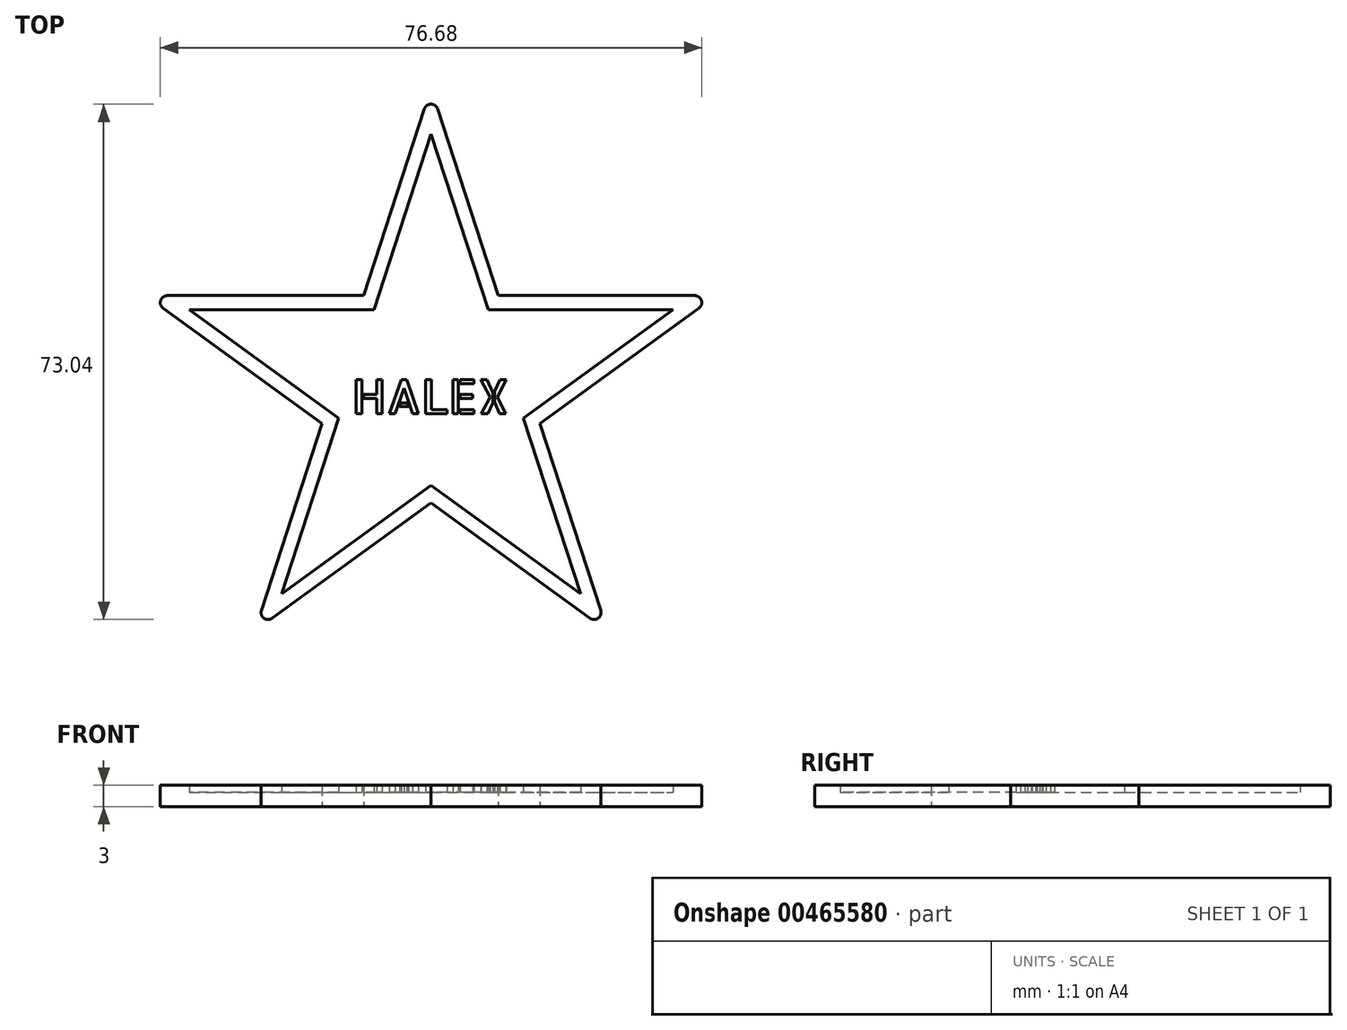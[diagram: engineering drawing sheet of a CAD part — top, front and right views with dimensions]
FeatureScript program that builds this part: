
annotation { "Feature Type Name" : "Feature", "Feature Type Description" : "" }
export const myFeature = defineFeature(function(context is Context, id is Id, definition is map)
    precondition{}
    {
        {
            var Q0;
            Q0=qCreatedBy(makeId("Top.planeOp"),FACE);
            var sketch = newSketch(context, id + "F0", { "sketchPlane" : qUnion([Q0])});
            skCircle(sketch, "E0.cCircle", {"center": v(0, 0) * mm, "radius": 15 * mm, "construction": true});
            skLineSegment(sketch, "E0.0", {"start": v(10.9, 15) * mm, "end": v(17.63, -5.73) * mm});
            skLineSegment(sketch, "E0.1", {"start": v(17.63, -5.73) * mm, "end": v(0, -18.54) * mm});
            skLineSegment(sketch, "E0.2", {"start": v(0, -18.54) * mm, "end": v(-17.63, -5.73) * mm});
            skLineSegment(sketch, "E0.3", {"start": v(-17.63, -5.73) * mm, "end": v(-10.9, 15) * mm});
            skLineSegment(sketch, "E0.4", {"start": v(-10.9, 15) * mm, "end": v(10.9, 15) * mm});
            skPoint(sketch, "E0.0.midPoint", {"position": v(14.27, 4.64) * mm});
            skLineSegment(sketch, "E1", {"start": v(-10.9, 15) * mm, "end": v(0, 36.03) * mm});
            skLineSegment(sketch, "E2", {"start": v(0, 36.03) * mm, "end": v(10.9, 15) * mm});
            skLineSegment(sketch, "E3", {"start": v(34.27, 11.13) * mm, "end": v(10.9, 15) * mm});
            skLineSegment(sketch, "E4", {"start": v(17.63, -5.73) * mm, "end": v(34.27, 11.13) * mm});
            skLineSegment(sketch, "E5", {"start": v(17.63, -5.73) * mm, "end": v(21.18, -29.15) * mm});
            skLineSegment(sketch, "E6", {"start": v(21.18, -29.15) * mm, "end": v(0, -18.54) * mm});
            skLineSegment(sketch, "E7", {"start": v(0, -18.54) * mm, "end": v(-21.18, -29.15) * mm});
            skLineSegment(sketch, "E8", {"start": v(-21.18, -29.15) * mm, "end": v(-17.63, -5.73) * mm});
            skLineSegment(sketch, "E9", {"start": v(-17.63, -5.73) * mm, "end": v(-34.27, 11.13) * mm});
            skLineSegment(sketch, "E10", {"start": v(-10.9, 15) * mm, "end": v(-34.27, 11.13) * mm});
            skSolve(sketch);
        }
        {
            var Q0;
            Q0=qCreatedBy(makeId("Top.planeOp"),FACE);
            var sketch = newSketch(context, id + "F1", { "sketchPlane" : qUnion([Q0])});
            skPoint(sketch, "E11.0", {"position": v(-34.27, 11.13) * mm});
            skPoint(sketch, "E12.0", {"position": v(34.27, 11.13) * mm});
            skPoint(sketch, "E13.0", {"position": v(21.18, -29.15) * mm});
            skPoint(sketch, "E14.0", {"position": v(-21.18, -29.15) * mm});
            skPoint(sketch, "E15.0", {"position": v(0, 36.03) * mm});
            skLineSegment(sketch, "E16", {"start": v(-34.27, 11.13) * mm, "end": v(34.27, 11.13) * mm});
            skLineSegment(sketch, "E17", {"start": v(-21.18, -29.15) * mm, "end": v(34.27, 11.13) * mm});
            skLineSegment(sketch, "E18", {"start": v(-21.18, -29.15) * mm, "end": v(0, 36.03) * mm});
            skLineSegment(sketch, "E19", {"start": v(0, 36.03) * mm, "end": v(21.18, -29.15) * mm});
            skLineSegment(sketch, "E20", {"start": v(21.18, -29.15) * mm, "end": v(-34.27, 11.13) * mm});
            skLineSegment(sketch, "E21.0", {"start": v(-40.42, 13.13) * mm, "end": v(40.42, 13.13) * mm});
            skLineSegment(sketch, "E21.1", {"start": v(24.98, -34.38) * mm, "end": v(-40.42, 13.13) * mm});
            skLineSegment(sketch, "E22.0", {"start": v(0, 42.5) * mm, "end": v(24.98, -34.38) * mm});
            skLineSegment(sketch, "E22.1", {"start": v(-24.98, -34.38) * mm, "end": v(0, 42.5) * mm});
            skLineSegment(sketch, "E23.0", {"start": v(-24.98, -34.38) * mm, "end": v(40.42, 13.13) * mm});
            skSolve(sketch);
        }
        {
            var Q0;
            {var subQ1=sQuery(id+"F1.wireOp",EDGE,"E16");var subQ5=sQuery(id+"F1.wireOp",EDGE,"E18");var subQ6=makeQuery(id+"F1.imprint","INTERSECT",VERTEX,{"derivedFrom":[subQ1,subQ5]});Q0=makeQuery(id+"F1.imprint","IMPRINT",FACE,{"disambiguationData":[TD([[makeQuery(id+"F1.imprint","IMPRINT",EDGE,{"disambiguationData":[TD([[subQ6,-1.0]])],"derivedFrom":subQ1}),-1.0]])]});}
            var Q1;
            {var subQ0=sQuery(id+"F1.wireOp",EDGE,"E20");var subQ1=sQuery(id+"F1.wireOp",EDGE,"E16");var subQ2=makeQuery(id+"F1.imprint","INTERSECT",VERTEX,{"derivedFrom":[subQ1,subQ0]});Q1=makeQuery(id+"F1.imprint","IMPRINT",FACE,{"disambiguationData":[TD([[makeQuery(id+"F1.imprint","IMPRINT",EDGE,{"disambiguationData":[TD([[subQ2,-1.0]])],"derivedFrom":subQ1}),-1.0]])]});}
            var Q2;
            {var subQ0=sQuery(id+"F1.wireOp",EDGE,"E22.1");var subQ1=sQuery(id+"F1.wireOp",EDGE,"E16");var subQ2=makeQuery(id+"F1.imprint","INTERSECT",VERTEX,{"derivedFrom":[subQ1,subQ0]});Q2=makeQuery(id+"F1.imprint","IMPRINT",FACE,{"disambiguationData":[TD([[makeQuery(id+"F1.imprint","IMPRINT",EDGE,{"disambiguationData":[TD([[subQ2,-1.0]])],"derivedFrom":subQ1}),-1.0]])]});}
            var Q3;
            {var subQ0=sQuery(id+"F1.wireOp",EDGE,"E19");var subQ1=sQuery(id+"F1.wireOp",EDGE,"E18");var subQ2=makeQuery(id+"F1.imprint","INTERSECT",VERTEX,{"derivedFrom":[subQ1,subQ0]});Q3=makeQuery(id+"F1.imprint","IMPRINT",FACE,{"disambiguationData":[TD([[makeQuery(id+"F1.imprint","IMPRINT",EDGE,{"disambiguationData":[TD([[subQ2,1.0]])],"derivedFrom":subQ1}),-1.0]])]});}
            var Q4;
            {var subQ0=sQuery(id+"F1.wireOp",EDGE,"E18");var subQ1=sQuery(id+"F1.wireOp",EDGE,"E16");var subQ2=makeQuery(id+"F1.imprint","INTERSECT",VERTEX,{"derivedFrom":[subQ1,subQ0]});Q4=makeQuery(id+"F1.imprint","IMPRINT",FACE,{"disambiguationData":[TD([[makeQuery(id+"F1.imprint","IMPRINT",EDGE,{"disambiguationData":[TD([[subQ2,-1.0]])],"derivedFrom":subQ1}),1.0]])]});}
            var Q5;
            {var subQ0=sQuery(id+"F1.wireOp",EDGE,"E19");var subQ1=sQuery(id+"F1.wireOp",EDGE,"E16");var subQ2=makeQuery(id+"F1.imprint","INTERSECT",VERTEX,{"derivedFrom":[subQ1,subQ0]});Q5=makeQuery(id+"F1.imprint","IMPRINT",FACE,{"disambiguationData":[TD([[makeQuery(id+"F1.imprint","IMPRINT",EDGE,{"disambiguationData":[TD([[subQ2,-1.0]])],"derivedFrom":subQ1}),-1.0]])]});}
            var Q6;
            {var subQ0=sQuery(id+"F1.wireOp",EDGE,"E20");var subQ1=sQuery(id+"F1.wireOp",EDGE,"E17");var subQ2=makeQuery(id+"F1.imprint","INTERSECT",VERTEX,{"derivedFrom":[subQ1,subQ0]});Q6=makeQuery(id+"F1.imprint","IMPRINT",FACE,{"disambiguationData":[TD([[makeQuery(id+"F1.imprint","IMPRINT",EDGE,{"disambiguationData":[TD([[subQ2,-1.0]])],"derivedFrom":subQ1}),-1.0]])]});}
            var Q7;
            {var subQ0=sQuery(id+"F1.wireOp",EDGE,"E21.1");var subQ1=sQuery(id+"F1.wireOp",EDGE,"E17");var subQ2=makeQuery(id+"F1.imprint","INTERSECT",VERTEX,{"derivedFrom":[subQ1,subQ0]});Q7=makeQuery(id+"F1.imprint","IMPRINT",FACE,{"disambiguationData":[TD([[makeQuery(id+"F1.imprint","IMPRINT",EDGE,{"disambiguationData":[TD([[subQ2,-1.0]])],"derivedFrom":subQ1}),1.0]])]});}
            var Q8;
            {var subQ0=sQuery(id+"F1.wireOp",EDGE,"E18");var subQ1=sQuery(id+"F1.wireOp",EDGE,"E17");var subQ2=makeQuery(id+"F1.imprint","INTERSECT",VERTEX,{"derivedFrom":[subQ1,subQ0]});Q8=makeQuery(id+"F1.imprint","IMPRINT",FACE,{"disambiguationData":[TD([[makeQuery(id+"F1.imprint","IMPRINT",EDGE,{"disambiguationData":[TD([[subQ2,-1.0]])],"derivedFrom":subQ1}),1.0]])]});}
            var Q9;
            {var subQ0=sQuery(id+"F1.wireOp",EDGE,"E20");var subQ1=sQuery(id+"F1.wireOp",EDGE,"E19");var subQ2=makeQuery(id+"F1.imprint","INTERSECT",VERTEX,{"derivedFrom":[subQ1,subQ0]});Q9=makeQuery(id+"F1.imprint","IMPRINT",FACE,{"disambiguationData":[TD([[makeQuery(id+"F1.imprint","IMPRINT",EDGE,{"disambiguationData":[TD([[subQ2,1.0]])],"derivedFrom":subQ1}),-1.0]])]});}
            var Q10;
            {var subQ0=sQuery(id+"F1.wireOp",EDGE,"E17");var subQ1=sQuery(id+"F1.wireOp",EDGE,"E16");var subQ2=makeQuery(id+"F1.imprint","INTERSECT",VERTEX,{"derivedFrom":[subQ1,subQ0]});Q10=makeQuery(id+"F1.imprint","IMPRINT",FACE,{"disambiguationData":[TD([[makeQuery(id+"F1.imprint","IMPRINT",EDGE,{"disambiguationData":[TD([[subQ2,1.0]])],"derivedFrom":subQ1}),-1.0]])]});}
            extrude(context, id + "F2", {"entities" : qUnion([Q0, Q1, Q2, Q3, Q4, Q5, Q6, Q7, Q8, Q9, Q10]), "depth" : 2 * mm});
        }
        {
            var Q0;
            {var subQ3=sQuery(id+"F1.wireOp",EDGE,"E19");var subQ7=sQuery(id+"F1.wireOp",EDGE,"E18");var subQ9=makeQuery(id+"F1.imprint","INTERSECT",VERTEX,{"derivedFrom":[subQ7,subQ3]});Q0=makeQuery(id+"F1.imprint","IMPRINT",FACE,{"disambiguationData":[TD([[makeQuery(id+"F1.imprint","IMPRINT",EDGE,{"disambiguationData":[TD([[subQ9,1.0]])],"derivedFrom":subQ7}),1.0]])]});}
            var Q1;
            {var subQ5=sQuery(id+"F1.wireOp",EDGE,"E20");var subQ6=sQuery(id+"F1.wireOp",EDGE,"E16");var subQ7=makeQuery(id+"F1.imprint","INTERSECT",VERTEX,{"derivedFrom":[subQ6,subQ5]});Q1=makeQuery(id+"F1.imprint","IMPRINT",FACE,{"disambiguationData":[TD([[makeQuery(id+"F1.imprint","IMPRINT",EDGE,{"disambiguationData":[TD([[subQ7,-1.0]])],"derivedFrom":subQ6}),1.0]])]});}
            var Q2;
            {var subQ3=sQuery(id+"F1.wireOp",EDGE,"E16");var subQ7=sQuery(id+"F1.wireOp",EDGE,"E17");var subQ8=makeQuery(id+"F1.imprint","INTERSECT",VERTEX,{"derivedFrom":[subQ3,subQ7]});Q2=makeQuery(id+"F1.imprint","IMPRINT",FACE,{"disambiguationData":[TD([[makeQuery(id+"F1.imprint","IMPRINT",EDGE,{"disambiguationData":[TD([[subQ8,1.0]])],"derivedFrom":subQ3}),1.0]])]});}
            var Q3;
            {var subQ3=sQuery(id+"F1.wireOp",EDGE,"E18");var subQ7=sQuery(id+"F1.wireOp",EDGE,"E17");var subQ9=makeQuery(id+"F1.imprint","INTERSECT",VERTEX,{"derivedFrom":[subQ7,subQ3]});Q3=makeQuery(id+"F1.imprint","IMPRINT",FACE,{"disambiguationData":[TD([[makeQuery(id+"F1.imprint","IMPRINT",EDGE,{"disambiguationData":[TD([[subQ9,-1.0]])],"derivedFrom":subQ7}),-1.0]])]});}
            var Q4;
            {var subQ5=sQuery(id+"F1.wireOp",EDGE,"E20");var subQ6=sQuery(id+"F1.wireOp",EDGE,"E19");var subQ7=makeQuery(id+"F1.imprint","INTERSECT",VERTEX,{"derivedFrom":[subQ6,subQ5]});Q4=makeQuery(id+"F1.imprint","IMPRINT",FACE,{"disambiguationData":[TD([[makeQuery(id+"F1.imprint","IMPRINT",EDGE,{"disambiguationData":[TD([[subQ7,1.0]])],"derivedFrom":subQ6}),1.0]])]});}
            var Q5;
            {var subQ0=sQuery(id+"F1.wireOp",EDGE,"E21.1");var subQ1=sQuery(id+"F1.wireOp",EDGE,"E17");var subQ2=makeQuery(id+"F1.imprint","INTERSECT",VERTEX,{"derivedFrom":[subQ1,subQ0]});Q5=makeQuery(id+"F1.imprint","IMPRINT",FACE,{"disambiguationData":[TD([[makeQuery(id+"F1.imprint","IMPRINT",EDGE,{"disambiguationData":[TD([[subQ2,-1.0]])],"derivedFrom":subQ1}),-1.0]])]});}
            var Q6;
            {var subQ0=sQuery(id+"F1.wireOp",EDGE,"E21.1");var subQ1=sQuery(id+"F1.wireOp",EDGE,"E18");var subQ2=makeQuery(id+"F1.imprint","INTERSECT",VERTEX,{"derivedFrom":[subQ1,subQ0]});Q6=makeQuery(id+"F1.imprint","IMPRINT",FACE,{"disambiguationData":[TD([[makeQuery(id+"F1.imprint","IMPRINT",EDGE,{"disambiguationData":[TD([[subQ2,-1.0]])],"derivedFrom":subQ1}),1.0]])]});}
            var Q7;
            {var subQ0=sQuery(id+"F1.wireOp",EDGE,"E22.1");var subQ1=sQuery(id+"F1.wireOp",EDGE,"E16");var subQ2=makeQuery(id+"F1.imprint","INTERSECT",VERTEX,{"derivedFrom":[subQ1,subQ0]});Q7=makeQuery(id+"F1.imprint","IMPRINT",FACE,{"disambiguationData":[TD([[makeQuery(id+"F1.imprint","IMPRINT",EDGE,{"disambiguationData":[TD([[subQ2,-1.0]])],"derivedFrom":subQ1}),1.0]])]});}
            var Q8;
            {var subQ0=sQuery(id+"F1.wireOp",EDGE,"E19");var subQ1=sQuery(id+"F1.wireOp",EDGE,"E16");var subQ2=makeQuery(id+"F1.imprint","INTERSECT",VERTEX,{"derivedFrom":[subQ1,subQ0]});Q8=makeQuery(id+"F1.imprint","IMPRINT",FACE,{"disambiguationData":[TD([[makeQuery(id+"F1.imprint","IMPRINT",EDGE,{"disambiguationData":[TD([[subQ2,-1.0]])],"derivedFrom":subQ1}),1.0]])]});}
            var Q9;
            {var subQ0=sQuery(id+"F1.wireOp",EDGE,"E19");var subQ1=sQuery(id+"F1.wireOp",EDGE,"E17");var subQ2=makeQuery(id+"F1.imprint","INTERSECT",VERTEX,{"derivedFrom":[subQ1,subQ0]});Q9=makeQuery(id+"F1.imprint","IMPRINT",FACE,{"disambiguationData":[TD([[makeQuery(id+"F1.imprint","IMPRINT",EDGE,{"disambiguationData":[TD([[subQ2,-1.0]])],"derivedFrom":subQ1}),-1.0]])]});}
            extrude(context, id + "F3", {"entities" : qUnion([Q0, Q1, Q2, Q3, Q4, Q5, Q6, Q7, Q8, Q9]), "operationType" : NewBodyOperationType.ADD, "depth" : 3 * mm});
        }
        {
            var Q0;
            Q0=makeQuery(id+"F3.opExtrude","SWEPT_EDGE",EDGE,{"disambiguationData":[OSD([sQuery(id+"F1.wireOp",EDGE,"E21.1"),sQuery(id+"F1.wireOp",EDGE,"E22.0")])]});
            var Q1;
            Q1=makeQuery(id+"F3.opExtrude","SWEPT_EDGE",EDGE,{"disambiguationData":[OSD([sQuery(id+"F1.wireOp",EDGE,"E22.0"),sQuery(id+"F1.wireOp",EDGE,"E22.1")])]});
            var Q2;
            Q2=makeQuery(id+"F3.opExtrude","SWEPT_EDGE",EDGE,{"disambiguationData":[OSD([sQuery(id+"F1.wireOp",EDGE,"E21.0"),sQuery(id+"F1.wireOp",EDGE,"E23.0")])]});
            var Q3;
            Q3=makeQuery(id+"F3.opExtrude","SWEPT_EDGE",EDGE,{"disambiguationData":[OSD([sQuery(id+"F1.wireOp",EDGE,"E21.0"),sQuery(id+"F1.wireOp",EDGE,"E21.1")])]});
            var Q4;
            Q4=makeQuery(id+"F3.opExtrude","SWEPT_EDGE",EDGE,{"disambiguationData":[OSD([sQuery(id+"F1.wireOp",EDGE,"E22.1"),sQuery(id+"F1.wireOp",EDGE,"E23.0")])]});
            fillet(context, id + "F4", {"entities" : qUnion([Q0, Q1, Q2, Q3, Q4]), "radius" : 1 * mm, "tangentPropagation" : true, "allowEdgeOverflow" : false});
        }
        {
            var Q0;
            Q0=makeQuery(id+"F2.opExtrude","CAP_FACE",FACE,{"disambiguationData":[OSD([sQuery(id+"F1.wireOp",EDGE,"E16"),sQuery(id+"F1.wireOp",EDGE,"E17"),sQuery(id+"F1.wireOp",EDGE,"E18"),sQuery(id+"F1.wireOp",EDGE,"E19"),sQuery(id+"F1.wireOp",EDGE,"E20")])],"isStart":false});
            var sketch = newSketch(context, id + "F5", { "sketchPlane" : qUnion([Q0])});
            skLineSegment(sketch, "E24.bottom", {"start": v(-11.22, 8.21) * mm, "end": v(11.1, 8.21) * mm, "construction": true});
            skLineSegment(sketch, "E24.top", {"start": v(-11.22, -11.89) * mm, "end": v(11.1, -11.89) * mm, "construction": true});
            skLineSegment(sketch, "E24.left", {"start": v(-11.22, 8.21) * mm, "end": v(-11.22, -11.89) * mm, "construction": true});
            skLineSegment(sketch, "E24.right", {"start": v(11.1, 8.21) * mm, "end": v(11.1, -11.89) * mm, "construction": true});
            skText(sketch, "E25", { "text": "HALEX", "fontName": "AllertaStencil-Regular.ttf"});
            const initialGuessF5  = {"E25": [-0.01122, -0.0036, 1, 0, 0.00482]};
            skSetInitialGuess(sketch, initialGuessF5);
            skSolve(sketch);
        }
        {
            var Q0;
            Q0=makeQuery(id+"F5.imprint","IMPRINT",FACE,{"disambiguationData":[TD([[makeQuery(id+"F5.imprint","IMPRINT",EDGE,{"derivedFrom":sQuery(id+"F5.wireOp",EDGE,"E25.sketch_text.stroke-8")}),-1.0]])]});
            var Q1;
            Q1=makeQuery(id+"F5.imprint","IMPRINT",FACE,{"disambiguationData":[TD([[makeQuery(id+"F5.imprint","IMPRINT",EDGE,{"derivedFrom":sQuery(id+"F5.wireOp",EDGE,"E25.sketch_text.stroke-0")}),-1.0]])]});
            var Q2;
            Q2=makeQuery(id+"F5.imprint","IMPRINT",FACE,{"disambiguationData":[TD([[makeQuery(id+"F5.imprint","IMPRINT",EDGE,{"derivedFrom":sQuery(id+"F5.wireOp",EDGE,"E25.sketch_text.stroke-12")}),-1.0]])]});
            var Q3;
            Q3=makeQuery(id+"F5.imprint","IMPRINT",FACE,{"disambiguationData":[TD([[makeQuery(id+"F5.imprint","IMPRINT",EDGE,{"derivedFrom":sQuery(id+"F5.wireOp",EDGE,"E25.sketch_text.stroke-19")}),-1.0]])]});
            var Q4;
            Q4=makeQuery(id+"F5.imprint","IMPRINT",FACE,{"disambiguationData":[TD([[makeQuery(id+"F5.imprint","IMPRINT",EDGE,{"derivedFrom":sQuery(id+"F5.wireOp",EDGE,"E25.sketch_text.stroke-23")}),-1.0]])]});
            var Q5;
            Q5=makeQuery(id+"F5.imprint","IMPRINT",FACE,{"disambiguationData":[TD([[makeQuery(id+"F5.imprint","IMPRINT",EDGE,{"derivedFrom":sQuery(id+"F5.wireOp",EDGE,"E25.sketch_text.stroke-41")}),-1.0]])]});
            var Q6;
            Q6=makeQuery(id+"F5.imprint","IMPRINT",FACE,{"disambiguationData":[TD([[makeQuery(id+"F5.imprint","IMPRINT",EDGE,{"derivedFrom":sQuery(id+"F5.wireOp",EDGE,"E25.sketch_text.stroke-37")}),-1.0]])]});
            var Q7;
            Q7=makeQuery(id+"F5.imprint","IMPRINT",FACE,{"disambiguationData":[TD([[makeQuery(id+"F5.imprint","IMPRINT",EDGE,{"derivedFrom":sQuery(id+"F5.wireOp",EDGE,"E25.sketch_text.stroke-45")}),-1.0]])]});
            var Q8;
            Q8=makeQuery(id+"F5.imprint","IMPRINT",FACE,{"disambiguationData":[TD([[makeQuery(id+"F5.imprint","IMPRINT",EDGE,{"derivedFrom":sQuery(id+"F5.wireOp",EDGE,"E25.sketch_text.stroke-52")}),-1.0]])]});
            var Q9;
            Q9=makeQuery(id+"F5.imprint","IMPRINT",FACE,{"disambiguationData":[TD([[makeQuery(id+"F5.imprint","IMPRINT",EDGE,{"derivedFrom":sQuery(id+"F5.wireOp",EDGE,"E25.sketch_text.stroke-29")}),-1.0]])]});
            var Q10;
            Q10=makeQuery(id+"F5.imprint","IMPRINT",FACE,{"disambiguationData":[TD([[makeQuery(id+"F5.imprint","IMPRINT",EDGE,{"derivedFrom":sQuery(id+"F5.wireOp",EDGE,"E25.sketch_text.stroke-33")}),-1.0]])]});
            extrude(context, id + "F6", {"entities" : qUnion([Q0, Q1, Q2, Q3, Q4, Q5, Q6, Q7, Q8, Q9, Q10]), "operationType" : NewBodyOperationType.ADD, "depth" : 1 * mm});
        }
    });
